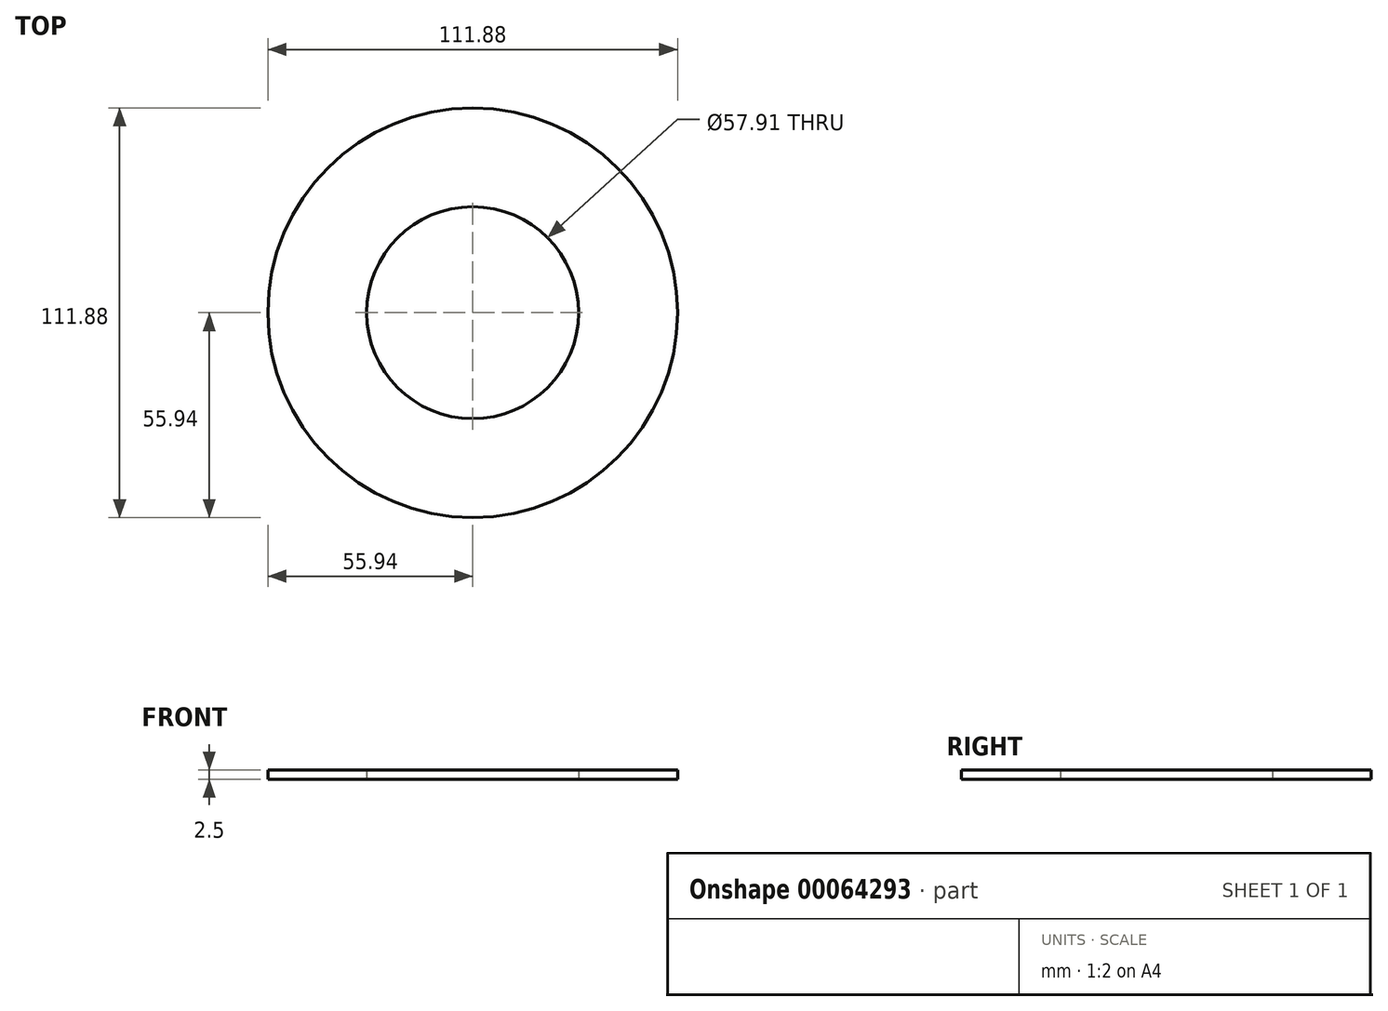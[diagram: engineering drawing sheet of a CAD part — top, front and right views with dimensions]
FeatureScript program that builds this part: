
annotation { "Feature Type Name" : "Feature", "Feature Type Description" : "" }
export const myFeature = defineFeature(function(context is Context, id is Id, definition is map)
    precondition{}
    {
        {
            var Q0;
            Q0=qCreatedBy(makeId("Top.planeOp"),FACE);
            var sketch = newSketch(context, id + "F0", { "sketchPlane" : qUnion([Q0])});
            skCircle(sketch, "E0", {"center": v(0, 0) * mm, "radius": 55.94 * mm});
            skCircle(sketch, "E1", {"center": v(0, 0) * mm, "radius": 28.96 * mm});
            skSolve(sketch);
        }
        {
            var Q0;
            Q0=makeQuery(id+"F0.imprint","IMPRINT",FACE,{"disambiguationData":[TD([[makeQuery(id+"F0.imprint","IMPRINT",EDGE,{"derivedFrom":sQuery(id+"F0.wireOp",EDGE,"E0")}),1.0]])]});
            extrude(context, id + "F1", {"entities" : qUnion([Q0]), "depth" : 2.5 * mm});
        }
    });
